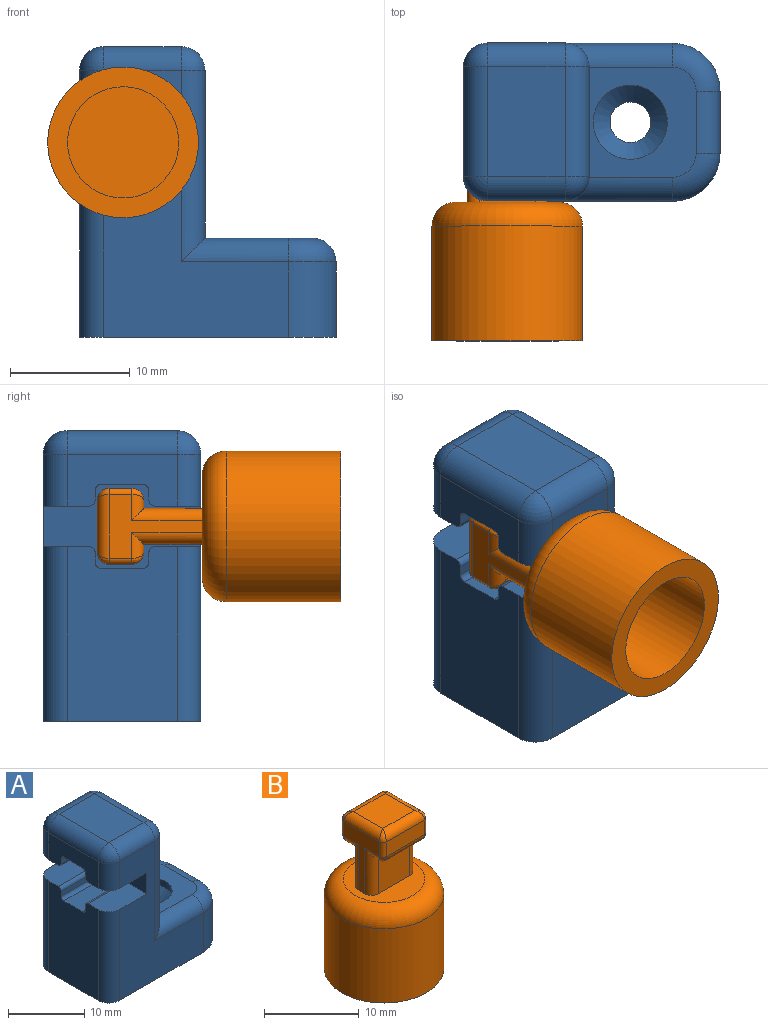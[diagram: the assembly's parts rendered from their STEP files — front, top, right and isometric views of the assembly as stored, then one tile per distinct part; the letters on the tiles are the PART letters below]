
ASSEMBLY  parts=2 mates=1
PART A: 57 faces, bbox 21.8x13.9x24.3 mm
  f0: plane 22.3x15.45mm, normal (0,1,0), area 184.3mm2, adj f4,f7,f8,f27,f33,f36,f37,f38
  f1: plane 14.6x9.2mm, normal (-1,0,0), area 126.2mm2, adj f3,f4,f7,f39,f41,f42,f43,f44
  f2: plane 22.3x15.45mm, normal (0,-1,0), area 184.3mm2, adj f3,f7,f10,f21,f23,f24,f25,f38
  f3: cylinder r=2mm len=14.6mm, axis (0,0,-1), area 45.9mm2, adj f1,f2,f7,f44
  f4: cylinder r=2mm len=14.6mm, axis (0,0,1), area 45.9mm2, adj f0,f1,f7,f39
  f5: plane 9.2x8.95mm, normal (0,0,1), area 50.4mm2, adj f17,f19,f23,f28,f31,f34,f36
  f6: cylinder r=1.7mm len=3.8mm, axis (0,0,-1), area 40.6mm2, adj f16,f18
  f7: plane 21.45x13.2mm, normal (0,0,-1), area 249.6mm2, adj f0,f1,f2,f3,f4,f8,f10,f11
  f8: cylinder r=4mm len=6.3mm, axis (0,0,-1), area 39.6mm2, adj f0,f7,f11,f34
  f9: plane 9.2x4.3mm, normal (-1,0,0), area 31.5mm2, adj f21,f26,f27,f40,f45,f46,f47,f48
  f10: cylinder r=4mm len=6.3mm, axis (0,0,-1), area 39.6mm2, adj f2,f7,f11,f28
  f11: plane 6.3x5.2mm, normal (1,0,0), area 32.8mm2, adj f7,f8,f10,f31
  f12: plane 5x2mm, normal (0,-1,0), area 10mm2, adj f7,f13,f15,f16
  f13: plane 5x2mm, normal (-1,0,0), area 10mm2, adj f7,f12,f14,f16
  f14: plane 5x2mm, normal (0,1,0), area 10mm2, adj f7,f13,f15,f16
  f15: plane 5x2mm, normal (1,0,0), area 10mm2, adj f7,f12,f14,f16
  f16: plane 5x5mm, normal (0,0,-1), area 15.9mm2, adj f6,f12,f13,f14,f15
  f17: cylinder r=3.1mm len=6.2mm, axis (0,0,1), area 21.4mm2, adj f5,f18
  f18: cone r=1.7mm half-angle=45deg, axis (0,0,1), area 29.9mm2, adj f6,f17
  f19: plane 14x9.2mm, normal (1,0,0), area 128.8mm2, adj f5,f24,f32,f37
  f20: plane 9.2x6.5mm, normal (0,0,1), area 59.8mm2, adj f25,f26,f32,f33
  f21: cylinder r=2mm len=4.3mm, axis (0,0,-1), area 13.5mm2, adj f2,f9,f22,f45
  f22: sphere r=2mm, area 6.3mm2, adj f21,f25,f26
  f23: cylinder r=2mm len=8.95mm, axis (-1,0,0), area 24.1mm2, adj f2,f5,f24,f28
  f24: cylinder r=2mm len=16mm, axis (0,0,-1), area 46.3mm2, adj f2,f19,f23,f29
  f25: cylinder r=2mm len=6.5mm, axis (-1,0,0), area 20.4mm2, adj f2,f20,f22,f29
  f26: cylinder r=2mm len=9.2mm, axis (0,1,0), area 28.9mm2, adj f9,f20,f22,f30
  f27: cylinder r=2mm len=4.3mm, axis (0,0,1), area 13.5mm2, adj f0,f9,f30,f40
  f28: torus R=2mm, axis (0,0,1), area 16.2mm2, adj f5,f10,f23,f31
  f29: sphere r=2mm, area 6.3mm2, adj f24,f25,f32
  f30: sphere r=2mm, area 6.3mm2, adj f26,f27,f33
  f31: cylinder r=2mm len=5.2mm, axis (0,-1,0), area 16.3mm2, adj f5,f11,f28,f34
  f32: cylinder r=2mm len=9.2mm, axis (0,-1,0), area 28.9mm2, adj f19,f20,f29,f35
  f33: cylinder r=2mm len=6.5mm, axis (1,0,0), area 20.4mm2, adj f0,f20,f30,f35
  f34: torus R=2mm, axis (0,0,1), area 16.2mm2, adj f5,f8,f31,f36
  f35: sphere r=2mm, area 6.3mm2, adj f32,f33,f37
  f36: cylinder r=2mm len=8.95mm, axis (1,0,0), area 24.1mm2, adj f0,f5,f34,f37
  f37: cylinder r=2mm len=16mm, axis (0,0,1), area 46.3mm2, adj f0,f19,f35,f36
  f38: plane 13.2x7mm, normal (-1,0,0), area 61.1mm2, adj f0,f2,f39,f40,f41,f42,f43,f44
  f39: plane 7x3.85mm, normal (0,0,1), area 26.1mm2, adj f0,f1,f4,f38,f50
  f40: plane 7x3.85mm, normal (0,0,-1), area 26.1mm2, adj f0,f9,f27,f38,f49
  f41: plane 7x0.8mm, normal (0,-1,0), area 5.6mm2, adj f1,f38,f50,f51
  f42: plane 7x3.5mm, normal (0,0,1), area 24.5mm2, adj f1,f38,f51,f52
  f43: plane 7x0.8mm, normal (0,1,0), area 5.6mm2, adj f1,f38,f52,f53
  f44: plane 7x3.85mm, normal (0,0,1), area 26.1mm2, adj f1,f2,f3,f38,f53
  f45: plane 7x3.85mm, normal (0,0,-1), area 26.1mm2, adj f2,f9,f21,f38,f54
  f46: plane 7x0.8mm, normal (0,1,0), area 5.6mm2, adj f9,f38,f54,f55
  f47: plane 7x3.5mm, normal (0,0,-1), area 24.5mm2, adj f9,f38,f55,f56
  f48: plane 7x0.8mm, normal (0,-1,0), area 5.6mm2, adj f9,f38,f49,f56
  f49: cylinder r=0.5mm len=7mm, axis (1,0,0), area 5.5mm2, adj f9,f38,f40,f48
  f50: cylinder r=0.5mm len=7mm, axis (-1,0,0), area 5.5mm2, adj f1,f38,f39,f41
  f51: cylinder r=0.5mm len=7mm, axis (1,0,0), area 5.5mm2, adj f1,f38,f41,f42
  f52: cylinder r=0.5mm len=7mm, axis (-1,0,0), area 5.5mm2, adj f1,f38,f42,f43
  f53: cylinder r=0.5mm len=7mm, axis (1,0,0), area 5.5mm2, adj f1,f38,f43,f44
  f54: cylinder r=0.5mm len=7mm, axis (-1,0,0), area 5.5mm2, adj f9,f38,f45,f46
  f55: cylinder r=0.5mm len=7mm, axis (1,0,0), area 5.5mm2, adj f9,f38,f46,f47
  f56: cylinder r=0.5mm len=7mm, axis (-1,0,0), area 5.5mm2, adj f9,f38,f47,f48
PART B: 41 faces, bbox 13.6x13.6x20.4 mm
  f0: plane 8.6x8.6mm, normal (0,0,1), area 38.8mm2, adj f5,f6,f7,f8,f9,f10,f11,f12
  f1: cylinder r=4.65mm len=9.5mm, axis (0,0,-1), area 277.6mm2, adj f3,f4
  f2: cylinder r=6.3mm len=12.6mm, axis (0,0,-1), area 380mm2, adj f3,f5
  f3: plane 12.6x12.6mm, normal (0,0,-1), area 56.8mm2, adj f1,f2
  f4: plane 9.3x9.3mm, normal (0,0,-1), area 67.9mm2, adj f1
  f5: torus R=4.3mm, axis (0,0,1), area 110mm2, adj f0,f2
  f6: plane 4.88x4.7mm, normal (0,-1,0), area 22.9mm2, adj f0,f7,f13,f22
  f7: cylinder r=1mm len=5.88mm, axis (0,0,-1), area 8.2mm2, adj f0,f6,f8,f40
  f8: plane 7.78x5.35mm, normal (1,0,0), area 16mm2, adj f0,f7,f9,f15,f20,f26,f35,f40
  f9: cylinder r=1mm len=5.88mm, axis (0,0,-1), area 8.2mm2, adj f0,f8,f10,f35
  f10: plane 4.88x4.7mm, normal (0,1,0), area 22.9mm2, adj f0,f9,f11,f14
  f11: cylinder r=1mm len=5.88mm, axis (0,0,-1), area 8.2mm2, adj f0,f10,f12,f31
  f12: plane 7.78x5.35mm, normal (-1,0,0), area 16mm2, adj f0,f11,f13,f17,f18,f27,f31,f36
  f13: cylinder r=1mm len=5.88mm, axis (0,0,-1), area 8.2mm2, adj f0,f6,f12,f36
  f14: plane 4.7x0.68mm, normal (0,0,-1), area 3.2mm2, adj f10,f31,f33,f35
  f15: cylinder r=0.5mm len=1.9mm, axis (0,0,-1), area 1.5mm2, adj f8,f16,f28,f34
  f16: plane 5.7x1.9mm, normal (0,1,0), area 10.8mm2, adj f15,f17,f30,f33
  f17: cylinder r=0.5mm len=1.9mm, axis (0,0,-1), area 1.5mm2, adj f12,f16,f29,f32
  f18: cylinder r=0.5mm len=1.9mm, axis (0,0,-1), area 1.5mm2, adj f12,f19,f25,f37
  f19: plane 5.7x1.9mm, normal (0,-1,0), area 10.8mm2, adj f18,f20,f23,f38
  f20: cylinder r=0.5mm len=1.9mm, axis (0,0,-1), area 1.5mm2, adj f8,f19,f24,f39
  f21: plane 4.7x4.35mm, normal (0,0,1), area 20.4mm2, adj f23,f26,f27,f30
  f22: plane 4.7x0.68mm, normal (0,0,-1), area 3.2mm2, adj f6,f36,f38,f40
  f23: cylinder r=1mm len=5.7mm, axis (-1,0,0), area 8.4mm2, adj f19,f21,f24,f25
  f24: bspline ~1.19x1mm, area 0.8mm2, adj f20,f23,f26
  f25: bspline ~1.19x1mm, area 0.8mm2, adj f18,f23,f27
  f26: cylinder r=1mm len=5.35mm, axis (0,-1,0), area 7.8mm2, adj f8,f21,f24,f28
  f27: cylinder r=1mm len=5.35mm, axis (0,1,0), area 7.8mm2, adj f12,f21,f25,f29
  f28: bspline ~1.19x1mm, area 0.8mm2, adj f15,f26,f30
  f29: bspline ~1.19x1mm, area 0.8mm2, adj f17,f27,f30
  f30: cylinder r=1mm len=5.7mm, axis (1,0,0), area 8.4mm2, adj f16,f21,f28,f29
  f31: cylinder r=1mm len=2.18mm, axis (0,-1,0), area 2.1mm2, adj f11,f12,f14,f32
  f32: bspline ~1.19x1mm, area 0.8mm2, adj f17,f31,f33
  f33: cylinder r=1mm len=5.7mm, axis (-1,0,0), area 8.4mm2, adj f14,f16,f32,f34
  f34: bspline ~1.19x1mm, area 0.8mm2, adj f15,f33,f35
  f35: cylinder r=1mm len=2.18mm, axis (0,1,0), area 2.1mm2, adj f8,f9,f14,f34
  f36: cylinder r=1mm len=2.18mm, axis (0,-1,0), area 2.1mm2, adj f12,f13,f22,f37
  f37: bspline ~1.19x1mm, area 0.8mm2, adj f18,f36,f38
  f38: cylinder r=1mm len=5.7mm, axis (1,0,0), area 8.4mm2, adj f19,f22,f37,f39
  f39: bspline ~1.19x1mm, area 0.8mm2, adj f20,f38,f40
  f40: cylinder r=1mm len=2.18mm, axis (0,1,0), area 2.1mm2, adj f7,f8,f22,f39
PLACE A t=(0,-0.3,-0.05)mm
PLACE B rot(axis=(-1,0,0),90deg) t=(-7.07,-18.6,16.25)mm
MATE fastened B.f8 <-> A.f38  axis (1,0,0) through (-3.72,-1.6,16.25)mm
